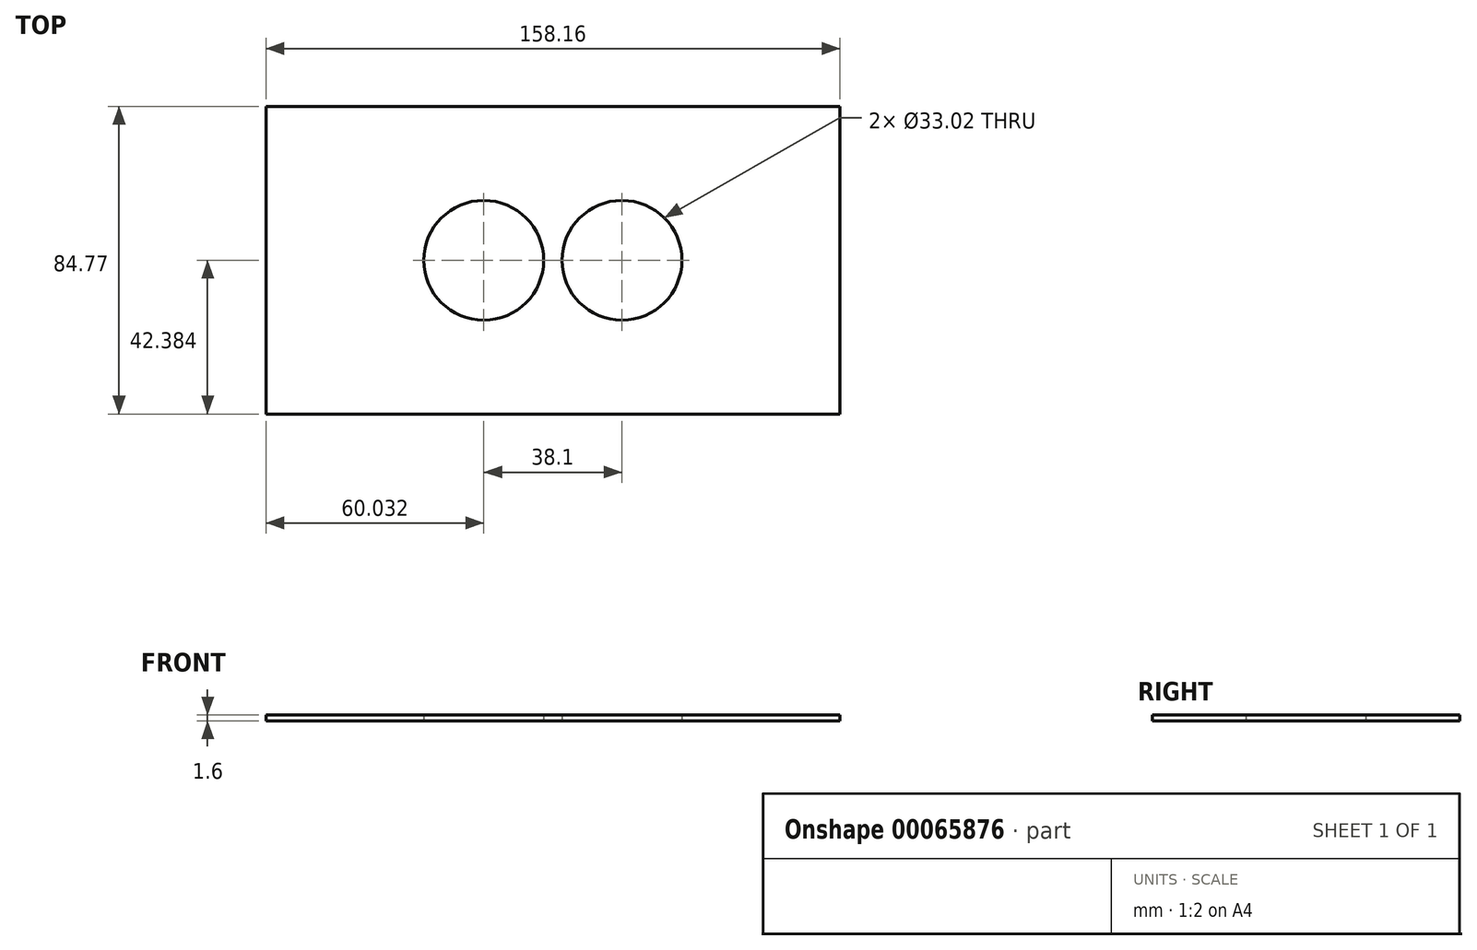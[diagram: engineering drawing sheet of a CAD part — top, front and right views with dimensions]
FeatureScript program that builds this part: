
annotation { "Feature Type Name" : "Feature", "Feature Type Description" : "" }
export const myFeature = defineFeature(function(context is Context, id is Id, definition is map)
    precondition{}
    {
        {
            var Q0;
            Q0=qCreatedBy(makeId("Top.planeOp"),FACE);
            var sketch = newSketch(context, id + "F0", { "sketchPlane" : qUnion([Q0])});
            skCircle(sketch, "E0", {"center": v(-3.56, 5.8) * mm, "radius": 16.51 * mm});
            skCircle(sketch, "E1", {"center": v(34.54, 5.8) * mm, "radius": 16.51 * mm});
            skLineSegment(sketch, "E2.bottom", {"start": v(-63.59, 48.18) * mm, "end": v(94.57, 48.18) * mm});
            skLineSegment(sketch, "E2.top", {"start": v(-63.59, -36.59) * mm, "end": v(94.57, -36.59) * mm});
            skLineSegment(sketch, "E2.left", {"start": v(-63.59, 48.18) * mm, "end": v(-63.59, -36.59) * mm});
            skLineSegment(sketch, "E2.right", {"start": v(94.57, 48.18) * mm, "end": v(94.57, -36.59) * mm});
            skLineSegment(sketch, "E3", {"start": v(-63.59, 5.8) * mm, "end": v(94.57, 5.8) * mm, "construction": true});
            skLineSegment(sketch, "E4", {"start": v(15.5, 48.18) * mm, "end": v(15.5, -36.59) * mm, "construction": true});
            skSolve(sketch);
        }
        {
            var Q0;
            Q0 = qSketchRegion(id + "F0", true);
            extrude(context, id + "F1", {"entities" : qUnion([Q0]), "depth" : 1.6 * mm});
        }
    });
